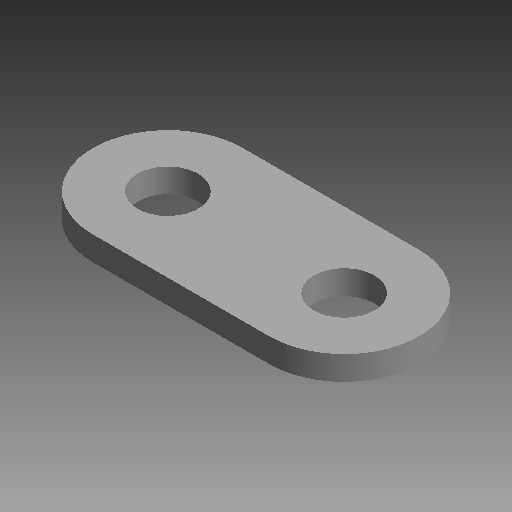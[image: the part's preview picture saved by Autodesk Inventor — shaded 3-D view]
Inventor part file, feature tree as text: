
AUTODESK INVENTOR PART (.ipt)
format: ipt  version: 2019 (Build 230136000, 136)  size: 100,352 bytes
history: native  units: mm (DEFAULTED — no unit token found)
features: other x14, extrude x1, sketch x1
ambient origin geometry x8: Origin, YZ Plane, XZ Plane, XY Plane, X Axis, Y Axis, Z Axis, Center Point
bodies: Solid1 (feature_tree)
feature tree (16):
  extrude  "Extrusion1"  [1 undecoded]
  other  "link_plate_XY"
  other  "link_plate_YZ"
  other  "link_plate_ZX"
  other  "link_plate_X"
  other  "link_plate_Y"
  other  "link_plate_Z"
  other  "link_plate_Center"
  other  "link_plate_b_XY"
  other  "link_plate_b_YZ"
  other  "link_plate_b_ZX"
  other  "link_plate_b_X"
  other  "link_plate_b_Y"
  other  "link_plate_b_Z"
  other  "link_plate_b_Center"
  sketch  "Sketch_4"  dims[d0=1.3mm d1=0.0mm]
note: 1 required parameter value undecoded (feature->parameter linkage not recoverable at this tier; creation-order binding heuristic only, values carry confidence <= 0.55)
